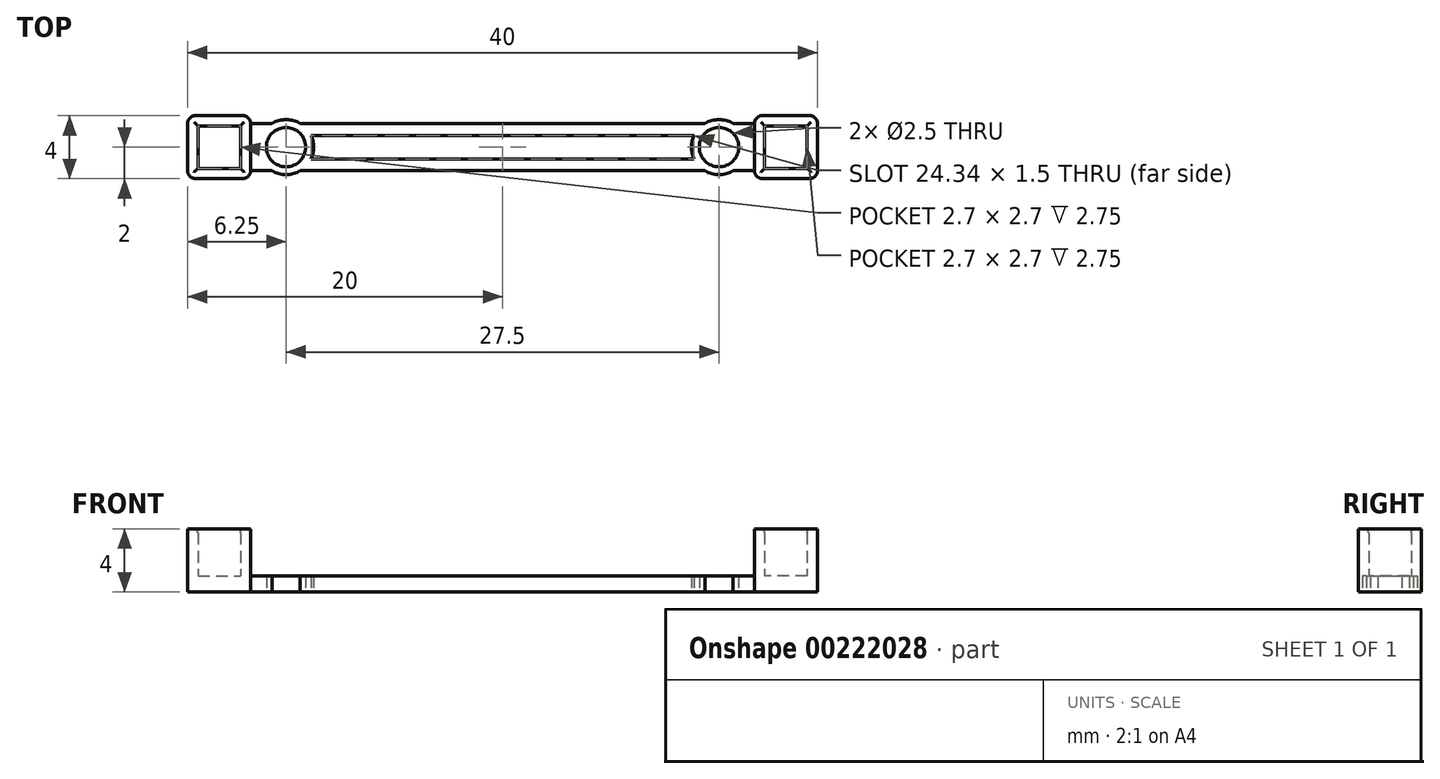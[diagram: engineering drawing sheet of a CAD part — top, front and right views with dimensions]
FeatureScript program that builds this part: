
annotation { "Feature Type Name" : "Feature", "Feature Type Description" : "" }
export const myFeature = defineFeature(function(context is Context, id is Id, definition is map)
    precondition{}
    {
        {
            var Q0;
            Q0=qCreatedBy(makeId("Top.planeOp"),FACE);
            var sketch = newSketch(context, id + "F0", { "sketchPlane" : qUnion([Q0])});
            skLineSegment(sketch, "E0", {"start": v(0, 0) * mm, "end": v(-13.75, 0) * mm, "construction": true});
            skLineSegment(sketch, "E1", {"start": v(0, 1.5) * mm, "end": v(-19.5, 1.5) * mm, "construction": true});
            skLineSegment(sketch, "E2", {"start": v(0, 1.5) * mm, "end": v(-19.5, 1.5) * mm});
            skLineSegment(sketch, "E3", {"start": v(-19.5, 1.5) * mm, "end": v(-19.5, -1.5) * mm});
            skLineSegment(sketch, "E4", {"start": v(-19.5, -1.5) * mm, "end": v(0, -1.5) * mm});
            skCircle(sketch, "E5", {"center": v(-13.75, 0) * mm, "radius": 1.25 * mm});
            skCircle(sketch, "E6", {"center": v(-13.75, 0) * mm, "radius": 1.75 * mm});
            skLineSegment(sketch, "E7", {"start": v(0, 0) * mm, "end": v(0, 0.75) * mm, "construction": true});
            skLineSegment(sketch, "E8", {"start": v(0, 0.75) * mm, "end": v(0, 0) * mm, "construction": true});
            skLineSegment(sketch, "E9", {"start": v(0, 0.75) * mm, "end": v(-12.17, 0.75) * mm});
            skLineSegment(sketch, "E10", {"start": v(0, -0.75) * mm, "end": v(-12.17, -0.75) * mm});
            skLineSegment(sketch, "E11", {"start": v(0, 0.75) * mm, "end": v(0, 1.5) * mm});
            skLineSegment(sketch, "E12", {"start": v(0, 0) * mm, "end": v(0, -0.75) * mm, "construction": true});
            skLineSegment(sketch, "E13", {"start": v(0, -0.75) * mm, "end": v(0, -1.5) * mm});
            skSolve(sketch);
        }
        {
            var Q0;
            Q0 = qSketchRegion(id + "F0", true);
            extrude(context, id + "F1", {"entities" : qUnion([Q0]), "depth" : 1 * mm});
        }
        {
            var Q0;
            Q0=makeQuery(id+"F1.opExtrude","CAP_FACE",FACE,{"disambiguationData":[OSD([sQuery(id+"F0.wireOp",EDGE,"E2"),sQuery(id+"F0.wireOp",EDGE,"E3"),sQuery(id+"F0.wireOp",EDGE,"E4"),sQuery(id+"F0.wireOp",EDGE,"E5"),sQuery(id+"F0.wireOp",EDGE,"2oN6Gx0w-HLV3-6Qr5-8PUt-cS9hU1NDVaQF")])],"isStart":false});
            var sketch = newSketch(context, id + "F2", { "sketchPlane" : qUnion([Q0])});
            skLineSegment(sketch, "E14", {"start": v(-19.5, 0) * mm, "end": v(-18, 0) * mm, "construction": true});
            skPoint(sketch, "E14.endSnap0", {"position": v(-19.5, 0) * mm});
            skLineSegment(sketch, "E15.bottom", {"start": v(-16.65, 1.35) * mm, "end": v(-19.35, 1.35) * mm});
            skLineSegment(sketch, "E15.top", {"start": v(-16.65, -1.35) * mm, "end": v(-19.35, -1.35) * mm});
            skLineSegment(sketch, "E15.left", {"start": v(-16.65, 1.35) * mm, "end": v(-16.65, -1.35) * mm});
            skLineSegment(sketch, "E15.right", {"start": v(-19.35, 1.35) * mm, "end": v(-19.35, -1.35) * mm});
            skPoint(sketch, "E15.middle", {"position": v(-18, 0) * mm});
            skLineSegment(sketch, "E16.bottom", {"start": v(-16, 2) * mm, "end": v(-20, 2) * mm});
            skLineSegment(sketch, "E16.top", {"start": v(-16, -2) * mm, "end": v(-20, -2) * mm});
            skLineSegment(sketch, "E16.left", {"start": v(-16, 2) * mm, "end": v(-16, -2) * mm});
            skLineSegment(sketch, "E16.right", {"start": v(-20, 2) * mm, "end": v(-20, -2) * mm});
            skSolve(sketch);
        }
        {
            var Q0;
            Q0 = qSketchRegion(id + "F2", true);
            extrude(context, id + "F3", {"entities" : qUnion([Q0]), "operationType" : NewBodyOperationType.ADD, "depth" : 3 * mm, "hasSecondDirection" : true, "secondDirectionOppositeDirection" : true, "secondDirectionDepth" : 1 * mm});
        }
        {
            var Q0;
            Q0=makeQuery(id+"F3.opExtrude","SWEPT_EDGE",EDGE,{"disambiguationData":[OSD([sQuery(id+"F2.wireOp",EDGE,"E16.top"),sQuery(id+"F2.wireOp",EDGE,"E16.left")])]});
            var Q1;
            Q1=makeQuery(id+"F3.opExtrude","SWEPT_EDGE",EDGE,{"disambiguationData":[OSD([sQuery(id+"F2.wireOp",EDGE,"E16.top"),sQuery(id+"F2.wireOp",EDGE,"E16.right")])]});
            var Q2;
            Q2=makeQuery(id+"F3.opExtrude","SWEPT_EDGE",EDGE,{"disambiguationData":[OSD([sQuery(id+"F2.wireOp",EDGE,"E16.bottom"),sQuery(id+"F2.wireOp",EDGE,"E16.left")])]});
            var Q3;
            Q3=makeQuery(id+"F3.opExtrude","SWEPT_EDGE",EDGE,{"disambiguationData":[OSD([sQuery(id+"F2.wireOp",EDGE,"E16.bottom"),sQuery(id+"F2.wireOp",EDGE,"E16.right")])]});
            fillet(context, id + "F4", {"entities" : qUnion([Q0, Q1, Q2, Q3]), "radius" : 0.5 * mm, "tangentPropagation" : true, "allowEdgeOverflow" : false});
        }
        {
            var Q0;
            Q0=makeQuery(id+"F3.opExtrude","CAP_EDGE",EDGE,{"disambiguationData":[OSD([sQuery(id+"F2.wireOp",EDGE,"E15.top")])],"isStart":false});
            var Q1;
            Q1=makeQuery(id+"F3.opExtrude","CAP_EDGE",EDGE,{"disambiguationData":[OSD([sQuery(id+"F2.wireOp",EDGE,"E15.left")])],"isStart":false});
            var Q2;
            Q2=makeQuery(id+"F3.opExtrude","CAP_EDGE",EDGE,{"disambiguationData":[OSD([sQuery(id+"F2.wireOp",EDGE,"E15.bottom")])],"isStart":false});
            var Q3;
            Q3=makeQuery(id+"F3.opExtrude","CAP_EDGE",EDGE,{"disambiguationData":[OSD([sQuery(id+"F2.wireOp",EDGE,"E15.right")])],"isStart":false});
            fillet(context, id + "F5", {"entities" : qUnion([Q0, Q1, Q2, Q3]), "radius" : 0.25 * mm, "tangentPropagation" : true, "allowEdgeOverflow" : false});
        }
        {
            var Q0;
            Q0=makeQuery(id+"F1.opExtrude","SWEPT_BODY",BODY,{"disambiguationData":[OSD([sQuery(id+"F0.wireOp",EDGE,"E2"),sQuery(id+"F0.wireOp",EDGE,"E3"),sQuery(id+"F0.wireOp",EDGE,"E4"),sQuery(id+"F0.wireOp",EDGE,"E5"),sQuery(id+"F0.wireOp",EDGE,"2oN6Gx0w-HLV3-6Qr5-8PUt-cS9hU1NDVaQF")])]});
            var Q1;
            Q1=qCreatedBy(makeId("Right.planeOp"),FACE);
            mirror(context, id + "F6", {"operationType" : NewBodyOperationType.ADD, "entities" : qUnion([Q0]), "mirrorPlane" : qUnion([Q1])});
        }
    });
